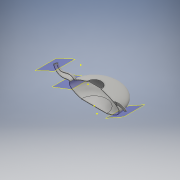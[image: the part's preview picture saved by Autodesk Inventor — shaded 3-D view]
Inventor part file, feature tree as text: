
AUTODESK INVENTOR PART (.ipt)
format: ipt  version: 2016 (Build 200138000, 138)  size: 560,128 bytes
history: native  units: in
note: dims shown in document units (in); Inventor stores cm internally (conversion verified against a paired STEP export)
features: sketch x10, delete_face x6, plane x3, other x2, surface_op x2, revolve x1, loft x1, shell x1, sweep x1
ambient origin geometry x8: Origin, YZ Plane, XZ Plane, XY Plane, X Axis, Y Axis, Z Axis, Center Point
bodies: Solid1 (feature_tree)
feature tree (27):
  other  "CrossSection1"
  revolve  "Revolution1"  [1 undecoded]
  sketch  "Sketch2"  dims[d3=0.0in d4=90.0deg d5=0.0in d6=90.0deg d7=0.0in d8=90.0deg]
  plane  "Work Plane1"
  sketch  "Sketch4"  dims[d14=0.1969in]
  sketch  "Sketch5"  dims[d15=0.0in]
  sketch  "Sketch6"
  plane  "Work Plane2"
  plane  "Work Plane3"
  loft  "Loft1"
  sketch  "Sketch9"
  shell  "Shell1"  Thickness=0.0in
  sweep  "Sweep1"
  delete_face  "Delete Face1"
  delete_face  "Delete Face2"
  surface_op  "Stitch Surface1"
  sketch  "Sketch10"
  delete_face  "Delete Face3"
  delete_face  "Delete Face4"
  delete_face  "Delete Face5"
  delete_face  "Delete Face6"
  sketch  "Sketch1"  dims[d0=90.0deg d1=0.0in d2=0.0in]
  sketch  "Sketch3"  dims[d9=0.02in d10=0.013in d11=0.5in d12=0.0in d13=2.0in]
  sketch  "Sketch7"
  sketch  "Sketch8"
  other  "Srf1"
  surface_op  "Boundary Patch1"
note: 1 required parameter value undecoded (feature->parameter linkage not recoverable at this tier; creation-order binding heuristic only, values carry confidence <= 0.55)
